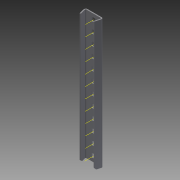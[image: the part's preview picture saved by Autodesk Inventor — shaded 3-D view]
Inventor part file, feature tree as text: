
AUTODESK INVENTOR PART (.ipt)
format: ipt  version: 2015 (Build 190159000, 159)  size: 402,432 bytes
history: native  units: in
note: dims shown in document units (in); Inventor stores cm internally (conversion verified against a paired STEP export)
features: other x16, boolean_combine x1, extrude x1, pattern_linear x1, imported_body x1, sketch x1
ambient origin geometry x8: Origin, YZ Plane, XZ Plane, XY Plane, X Axis, Y Axis, Z Axis, Center Point
bodies: Body1 (feature_tree)
feature tree (21):
  boolean_combine  "Combine1"
  other  "Linear Slide"
  other  "Work Axis1"
  extrude  "Extrusion1"  TaperAngle=0.0deg  [1 undecoded]
  pattern_linear  "Rectangular Pattern1"  Spacing1=0.0in  [1 undecoded]
  other  "bottom plane"
  other  "top plane"
  imported_body  "Base1"
  other  "Work Point1"
  other  "Work Axis2"
  sketch  "Sketch1"  dims[d0=4.7244in d2=0.5in d4=0.0in d5=0.0in d6=0.0in d8=0.0in]
  other  "Work Axis46"
  other  "Work Axis47"
  other  "Work Axis48"
  other  "Work Axis49"
  other  "Work Axis50"
  other  "Work Axis51"
  other  "Work Axis52"
  other  "Work Axis102"
  other  "Work Axis103"
  other  "Work Axis104"
note: 2 required parameter values undecoded (feature->parameter linkage not recoverable at this tier; creation-order binding heuristic only, values carry confidence <= 0.55)
